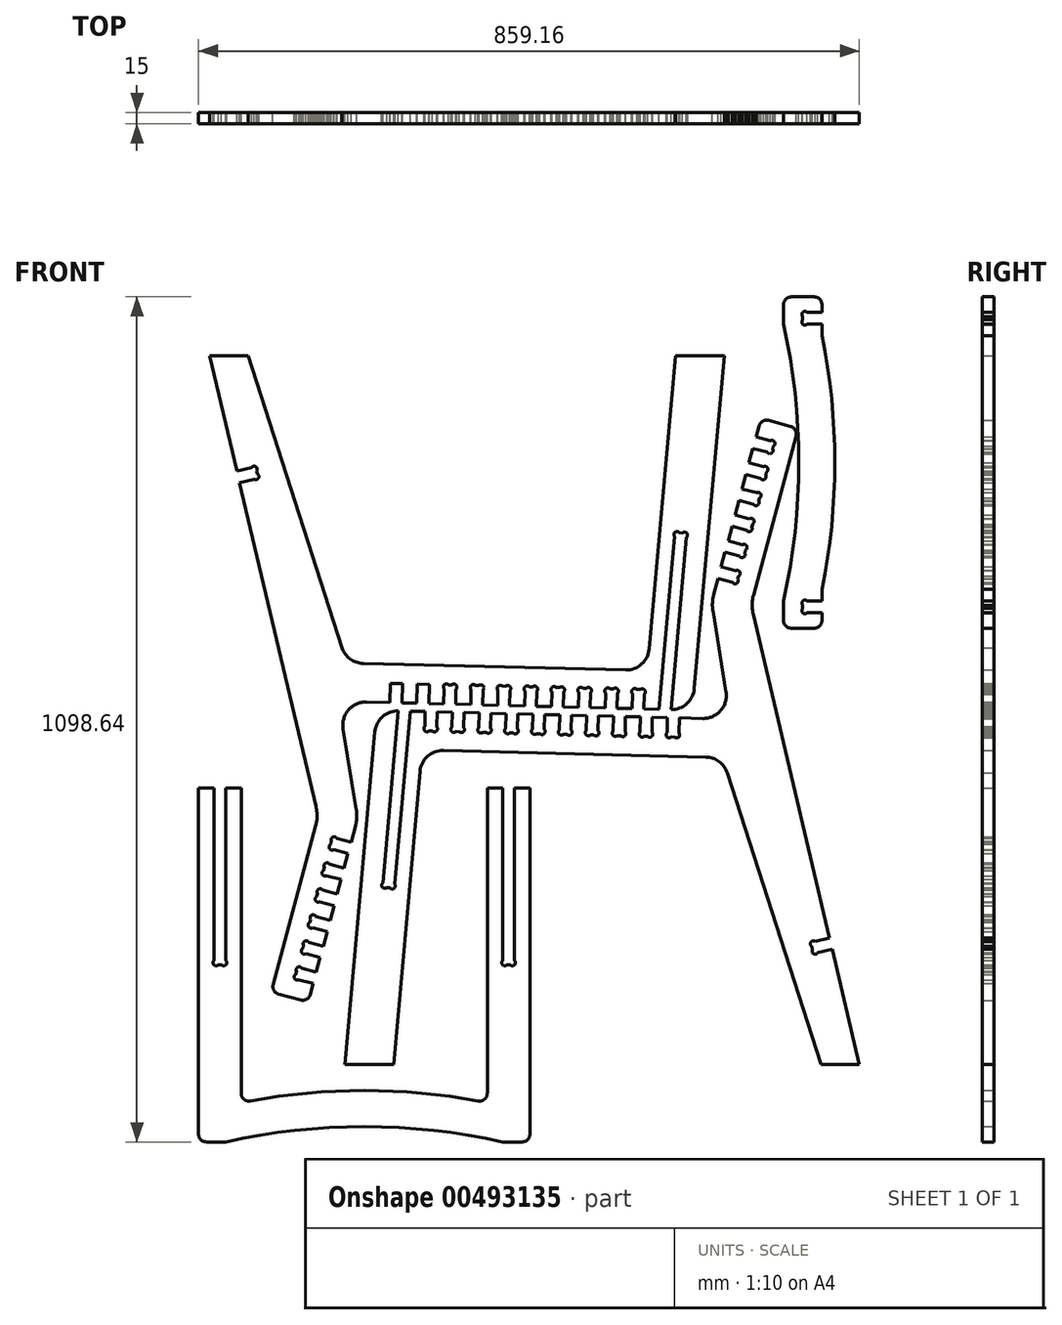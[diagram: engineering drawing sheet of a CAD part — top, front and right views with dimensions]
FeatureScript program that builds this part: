
annotation { "Feature Type Name" : "Feature", "Feature Type Description" : "" }
export const myFeature = defineFeature(function(context is Context, id is Id, definition is map)
    precondition{}
    {
        {
            var Q0;
            Q0=qCreatedBy(makeId("Front.planeOp"),FACE);
            var sketch = newSketch(context, id + "F0", { "sketchPlane" : qUnion([Q0])});
            skLineSegment(sketch, "E0", {"start": v(-375.2, 497.25) * mm, "end": v(-425.2, 497.25) * mm});
            skLineSegment(sketch, "E1", {"start": v(-425.2, 497.25) * mm, "end": v(-389.9, 347.46) * mm});
            skLineSegment(sketch, "E2", {"start": v(-389.9, 347.46) * mm, "end": v(-371.08, 351.9) * mm});
            skArc(sketch, "E3", {"start": v(-371.08, 351.9) * mm, "mid": v(-365.57, 353.2) * mm, "end": v(-364.28, 347.69) * mm});
            skLineSegment(sketch, "E4", {"start": v(-364.28, 347.69) * mm, "end": v(-363.34, 343.71) * mm});
            skArc(sketch, "E5", {"start": v(-363.34, 343.71) * mm, "mid": v(-362.04, 338.2) * mm, "end": v(-367.55, 336.91) * mm});
            skLineSegment(sketch, "E6", {"start": v(-367.55, 336.91) * mm, "end": v(-386.37, 332.48) * mm});
            skLineSegment(sketch, "E7", {"start": v(-386.37, 332.48) * mm, "end": v(-287.1, -88.96) * mm});
            skArc(sketch, "E8", {"start": v(-287.1, -88.96) * mm, "mid": v(-285.77, -101.18) * mm, "end": v(-287.47, -113.36) * mm});
            skLineSegment(sketch, "E9", {"start": v(-287.47, -113.36) * mm, "end": v(-342.89, -320.18) * mm});
            skArc(sketch, "E10", {"start": v(-342.89, -320.18) * mm, "mid": v(-341.89, -327.77) * mm, "end": v(-335.82, -332.42) * mm});
            skLineSegment(sketch, "E11", {"start": v(-335.82, -332.42) * mm, "end": v(-306.84, -340.19) * mm});
            skArc(sketch, "E12", {"start": v(-306.84, -340.19) * mm, "mid": v(-299.25, -339.19) * mm, "end": v(-294.6, -333.12) * mm});
            skLineSegment(sketch, "E13", {"start": v(-294.6, -333.12) * mm, "end": v(-290.77, -318.82) * mm});
            skLineSegment(sketch, "E14", {"start": v(-290.77, -318.82) * mm, "end": v(-309.45, -313.82) * mm});
            skArc(sketch, "E15", {"start": v(-309.45, -313.82) * mm, "mid": v(-314.91, -312.35) * mm, "end": v(-313.45, -306.9) * mm});
            skLineSegment(sketch, "E16", {"start": v(-313.45, -306.9) * mm, "end": v(-312.39, -302.94) * mm});
            skArc(sketch, "E17", {"start": v(-312.39, -302.94) * mm, "mid": v(-310.93, -297.48) * mm, "end": v(-305.46, -298.95) * mm});
            skLineSegment(sketch, "E18", {"start": v(-305.46, -298.95) * mm, "end": v(-286.78, -303.95) * mm});
            skLineSegment(sketch, "E19", {"start": v(-286.78, -303.95) * mm, "end": v(-281.7, -285.02) * mm});
            skLineSegment(sketch, "E20", {"start": v(-281.7, -285.02) * mm, "end": v(-300.39, -280.02) * mm});
            skArc(sketch, "E21", {"start": v(-300.39, -280.02) * mm, "mid": v(-305.85, -278.55) * mm, "end": v(-304.39, -273.09) * mm});
            skLineSegment(sketch, "E22", {"start": v(-304.39, -273.09) * mm, "end": v(-303.33, -269.14) * mm});
            skArc(sketch, "E23", {"start": v(-303.33, -269.14) * mm, "mid": v(-301.87, -263.68) * mm, "end": v(-296.4, -265.14) * mm});
            skLineSegment(sketch, "E24", {"start": v(-296.4, -265.14) * mm, "end": v(-277.72, -270.15) * mm});
            skLineSegment(sketch, "E25", {"start": v(-277.72, -270.15) * mm, "end": v(-272.65, -251.22) * mm});
            skLineSegment(sketch, "E26", {"start": v(-272.65, -251.22) * mm, "end": v(-291.33, -246.21) * mm});
            skArc(sketch, "E27", {"start": v(-291.33, -246.21) * mm, "mid": v(-296.8, -244.75) * mm, "end": v(-295.33, -239.29) * mm});
            skLineSegment(sketch, "E28", {"start": v(-295.33, -239.29) * mm, "end": v(-294.27, -235.34) * mm});
            skArc(sketch, "E29", {"start": v(-294.27, -235.34) * mm, "mid": v(-292.81, -229.88) * mm, "end": v(-287.35, -231.34) * mm});
            skLineSegment(sketch, "E30", {"start": v(-287.35, -231.34) * mm, "end": v(-268.66, -236.34) * mm});
            skLineSegment(sketch, "E31", {"start": v(-268.66, -236.34) * mm, "end": v(-263.6, -217.42) * mm});
            skLineSegment(sketch, "E32", {"start": v(-263.6, -217.42) * mm, "end": v(-282.27, -212.4) * mm});
            skArc(sketch, "E33", {"start": v(-282.27, -212.4) * mm, "mid": v(-287.74, -210.95) * mm, "end": v(-286.27, -205.48) * mm});
            skLineSegment(sketch, "E34", {"start": v(-286.27, -205.48) * mm, "end": v(-285.22, -201.54) * mm});
            skArc(sketch, "E35", {"start": v(-285.22, -201.54) * mm, "mid": v(-283.75, -196.07) * mm, "end": v(-278.29, -197.54) * mm});
            skLineSegment(sketch, "E36", {"start": v(-278.29, -197.54) * mm, "end": v(-259.6, -202.54) * mm});
            skLineSegment(sketch, "E37", {"start": v(-259.6, -202.54) * mm, "end": v(-254.54, -183.61) * mm});
            skLineSegment(sketch, "E38", {"start": v(-254.54, -183.61) * mm, "end": v(-273.22, -178.6) * mm});
            skArc(sketch, "E39", {"start": v(-273.22, -178.6) * mm, "mid": v(-278.68, -177.14) * mm, "end": v(-277.22, -171.68) * mm});
            skLineSegment(sketch, "E40", {"start": v(-277.22, -171.68) * mm, "end": v(-276.16, -167.73) * mm});
            skArc(sketch, "E41", {"start": v(-276.16, -167.73) * mm, "mid": v(-274.7, -162.27) * mm, "end": v(-269.23, -163.73) * mm});
            skLineSegment(sketch, "E42", {"start": v(-269.23, -163.73) * mm, "end": v(-250.55, -168.74) * mm});
            skLineSegment(sketch, "E43", {"start": v(-250.55, -168.74) * mm, "end": v(-245.48, -149.8) * mm});
            skLineSegment(sketch, "E44", {"start": v(-245.48, -149.8) * mm, "end": v(-264.16, -144.8) * mm});
            skArc(sketch, "E45", {"start": v(-264.16, -144.8) * mm, "mid": v(-269.62, -143.34) * mm, "end": v(-268.16, -137.88) * mm});
            skLineSegment(sketch, "E46", {"start": v(-268.16, -137.88) * mm, "end": v(-267.1, -133.93) * mm});
            skArc(sketch, "E47", {"start": v(-267.1, -133.93) * mm, "mid": v(-265.64, -128.47) * mm, "end": v(-260.17, -129.93) * mm});
            skLineSegment(sketch, "E48", {"start": v(-260.17, -129.93) * mm, "end": v(-241.5, -134.94) * mm});
            skLineSegment(sketch, "E49", {"start": v(-241.5, -134.94) * mm, "end": v(-235.8, -113.7) * mm});
            skArc(sketch, "E50", {"start": v(-235.8, -113.7) * mm, "mid": v(-234.15, -103.12) * mm, "end": v(-234.8, -92.43) * mm});
            skLineSegment(sketch, "E51", {"start": v(-234.8, -92.43) * mm, "end": v(-251.88, 12.44) * mm});
            skArc(sketch, "E52", {"start": v(-251.88, 12.44) * mm, "mid": v(-244.88, 36.98) * mm, "end": v(-221.53, 47.25) * mm});
            skLineSegment(sketch, "E53", {"start": v(-221.53, 47.25) * mm, "end": v(-190.95, 46.49) * mm});
            skLineSegment(sketch, "E54", {"start": v(-190.95, 46.49) * mm, "end": v(-190.33, 71.48) * mm});
            skLineSegment(sketch, "E55", {"start": v(-190.33, 71.48) * mm, "end": v(-174.93, 71.1) * mm});
            skLineSegment(sketch, "E56", {"start": v(-174.93, 71.1) * mm, "end": v(-175.56, 46.1) * mm});
            skLineSegment(sketch, "E57", {"start": v(-175.56, 46.1) * mm, "end": v(-155.97, 45.62) * mm});
            skLineSegment(sketch, "E58", {"start": v(-155.97, 45.62) * mm, "end": v(-155.34, 70.6) * mm});
            skLineSegment(sketch, "E59", {"start": v(-155.34, 70.6) * mm, "end": v(-139.95, 70.22) * mm});
            skLineSegment(sketch, "E60", {"start": v(-139.95, 70.22) * mm, "end": v(-140.57, 45.23) * mm});
            skLineSegment(sketch, "E61", {"start": v(-140.57, 45.23) * mm, "end": v(-120.98, 44.74) * mm});
            skLineSegment(sketch, "E62", {"start": v(-120.98, 44.74) * mm, "end": v(-120.5, 64.08) * mm});
            skArc(sketch, "E63", {"start": v(-120.5, 64.08) * mm, "mid": v(-120.36, 69.73) * mm, "end": v(-114.7, 69.6) * mm});
            skLineSegment(sketch, "E64", {"start": v(-114.7, 69.6) * mm, "end": v(-110.62, 69.5) * mm});
            skArc(sketch, "E65", {"start": v(-110.62, 69.5) * mm, "mid": v(-104.97, 69.35) * mm, "end": v(-105.1, 63.7) * mm});
            skLineSegment(sketch, "E66", {"start": v(-105.1, 63.7) * mm, "end": v(-105.59, 44.36) * mm});
            skLineSegment(sketch, "E67", {"start": v(-105.59, 44.36) * mm, "end": v(-86, 43.87) * mm});
            skLineSegment(sketch, "E68", {"start": v(-86, 43.87) * mm, "end": v(-85.51, 63.2) * mm});
            skArc(sketch, "E69", {"start": v(-85.51, 63.2) * mm, "mid": v(-85.37, 68.86) * mm, "end": v(-79.72, 68.72) * mm});
            skLineSegment(sketch, "E70", {"start": v(-79.72, 68.72) * mm, "end": v(-75.64, 68.62) * mm});
            skArc(sketch, "E71", {"start": v(-75.64, 68.62) * mm, "mid": v(-69.98, 68.48) * mm, "end": v(-70.12, 62.82) * mm});
            skLineSegment(sketch, "E72", {"start": v(-70.12, 62.82) * mm, "end": v(-70.6, 43.49) * mm});
            skLineSegment(sketch, "E73", {"start": v(-70.6, 43.49) * mm, "end": v(-51.01, 43) * mm});
            skLineSegment(sketch, "E74", {"start": v(-51.01, 43) * mm, "end": v(-50.53, 62.33) * mm});
            skArc(sketch, "E75", {"start": v(-50.53, 62.33) * mm, "mid": v(-50.39, 67.99) * mm, "end": v(-44.73, 67.85) * mm});
            skLineSegment(sketch, "E76", {"start": v(-44.73, 67.85) * mm, "end": v(-40.65, 67.75) * mm});
            skArc(sketch, "E77", {"start": v(-40.65, 67.75) * mm, "mid": v(-35, 67.6) * mm, "end": v(-35.14, 61.95) * mm});
            skLineSegment(sketch, "E78", {"start": v(-35.14, 61.95) * mm, "end": v(-35.62, 42.62) * mm});
            skLineSegment(sketch, "E79", {"start": v(-35.62, 42.62) * mm, "end": v(-16.03, 42.13) * mm});
            skLineSegment(sketch, "E80", {"start": v(-16.03, 42.13) * mm, "end": v(-15.55, 61.46) * mm});
            skArc(sketch, "E81", {"start": v(-15.55, 61.46) * mm, "mid": v(-15.4, 67.12) * mm, "end": v(-9.75, 66.98) * mm});
            skLineSegment(sketch, "E82", {"start": v(-9.75, 66.98) * mm, "end": v(-5.67, 66.87) * mm});
            skArc(sketch, "E83", {"start": v(-5.67, 66.87) * mm, "mid": v(-0.01, 66.73) * mm, "end": v(-0.15, 61.08) * mm});
            skLineSegment(sketch, "E84", {"start": v(-0.15, 61.08) * mm, "end": v(-0.63, 41.74) * mm});
            skLineSegment(sketch, "E85", {"start": v(-0.63, 41.74) * mm, "end": v(18.96, 41.26) * mm});
            skLineSegment(sketch, "E86", {"start": v(18.96, 41.26) * mm, "end": v(19.44, 60.6) * mm});
            skArc(sketch, "E87", {"start": v(19.44, 60.6) * mm, "mid": v(19.58, 66.24) * mm, "end": v(25.23, 66.1) * mm});
            skLineSegment(sketch, "E88", {"start": v(25.23, 66.1) * mm, "end": v(29.32, 66) * mm});
            skArc(sketch, "E89", {"start": v(29.32, 66) * mm, "mid": v(34.97, 65.86) * mm, "end": v(34.83, 60.2) * mm});
            skLineSegment(sketch, "E90", {"start": v(34.83, 60.2) * mm, "end": v(34.35, 40.87) * mm});
            skLineSegment(sketch, "E91", {"start": v(34.35, 40.87) * mm, "end": v(53.94, 40.38) * mm});
            skLineSegment(sketch, "E92", {"start": v(53.94, 40.38) * mm, "end": v(54.42, 59.72) * mm});
            skArc(sketch, "E93", {"start": v(54.42, 59.72) * mm, "mid": v(54.56, 65.37) * mm, "end": v(60.22, 65.23) * mm});
            skLineSegment(sketch, "E94", {"start": v(60.22, 65.23) * mm, "end": v(64.3, 65.13) * mm});
            skArc(sketch, "E95", {"start": v(64.3, 65.13) * mm, "mid": v(69.96, 64.99) * mm, "end": v(69.82, 59.33) * mm});
            skLineSegment(sketch, "E96", {"start": v(69.82, 59.33) * mm, "end": v(69.34, 40) * mm});
            skLineSegment(sketch, "E97", {"start": v(69.34, 40) * mm, "end": v(88.93, 39.51) * mm});
            skLineSegment(sketch, "E98", {"start": v(88.93, 39.51) * mm, "end": v(89.4, 58.85) * mm});
            skArc(sketch, "E99", {"start": v(89.4, 58.85) * mm, "mid": v(89.55, 64.5) * mm, "end": v(95.2, 64.36) * mm});
            skLineSegment(sketch, "E100", {"start": v(95.2, 64.36) * mm, "end": v(99.29, 64.26) * mm});
            skArc(sketch, "E101", {"start": v(99.29, 64.26) * mm, "mid": v(104.94, 64.12) * mm, "end": v(104.8, 58.46) * mm});
            skLineSegment(sketch, "E102", {"start": v(104.8, 58.46) * mm, "end": v(104.32, 39.13) * mm});
            skLineSegment(sketch, "E103", {"start": v(104.32, 39.13) * mm, "end": v(123.91, 38.64) * mm});
            skLineSegment(sketch, "E104", {"start": v(123.91, 38.64) * mm, "end": v(124.4, 57.97) * mm});
            skArc(sketch, "E105", {"start": v(124.4, 57.97) * mm, "mid": v(124.53, 63.63) * mm, "end": v(130.19, 63.49) * mm});
            skLineSegment(sketch, "E106", {"start": v(130.19, 63.49) * mm, "end": v(134.27, 63.39) * mm});
            skArc(sketch, "E107", {"start": v(134.27, 63.39) * mm, "mid": v(139.93, 63.24) * mm, "end": v(139.79, 57.6) * mm});
            skLineSegment(sketch, "E108", {"start": v(139.79, 57.6) * mm, "end": v(139.3, 38.26) * mm});
            skLineSegment(sketch, "E109", {"start": v(139.3, 38.26) * mm, "end": v(158.88, 37.77) * mm});
            skLineSegment(sketch, "E110", {"start": v(158.88, 37.77) * mm, "end": v(179.13, 262.38) * mm});
            skArc(sketch, "E111", {"start": v(179.13, 262.38) * mm, "mid": v(179.64, 268.01) * mm, "end": v(185.27, 267.5) * mm});
            skLineSegment(sketch, "E112", {"start": v(185.27, 267.5) * mm, "end": v(189.34, 267.14) * mm});
            skArc(sketch, "E113", {"start": v(189.34, 267.14) * mm, "mid": v(194.97, 266.63) * mm, "end": v(194.46, 261) * mm});
            skLineSegment(sketch, "E114", {"start": v(194.46, 261) * mm, "end": v(174.3, 37.38) * mm});
            skArc(sketch, "E115", {"start": v(174.3, 37.38) * mm, "mid": v(194.88, 45.05) * mm, "end": v(204.71, 64.68) * mm});
            skLineSegment(sketch, "E116", {"start": v(204.71, 64.68) * mm, "end": v(243.7, 497.25) * mm});
            skLineSegment(sketch, "E117", {"start": v(243.7, 497.25) * mm, "end": v(180.44, 497.25) * mm});
            skLineSegment(sketch, "E118", {"start": v(180.44, 497.25) * mm, "end": v(146.08, 116.15) * mm});
            skArc(sketch, "E119", {"start": v(146.08, 116.15) * mm, "mid": v(136.17, 96.45) * mm, "end": v(115.46, 88.86) * mm});
            skLineSegment(sketch, "E120", {"start": v(115.46, 88.86) * mm, "end": v(-225.61, 97.36) * mm});
            skArc(sketch, "E121", {"start": v(-225.61, 97.36) * mm, "mid": v(-242.67, 103.21) * mm, "end": v(-253.3, 117.79) * mm});
            skLineSegment(sketch, "E122", {"start": v(-253.3, 117.79) * mm, "end": v(-375.2, 497.25) * mm});
            skLineSegment(sketch, "E123", {"start": v(369.36, -424.14) * mm, "end": v(419.36, -424.14) * mm});
            skLineSegment(sketch, "E124", {"start": v(419.36, -424.14) * mm, "end": v(384.07, -274.36) * mm});
            skLineSegment(sketch, "E125", {"start": v(384.07, -274.36) * mm, "end": v(365.25, -278.8) * mm});
            skArc(sketch, "E126", {"start": v(365.25, -278.8) * mm, "mid": v(359.74, -280.09) * mm, "end": v(358.44, -274.58) * mm});
            skLineSegment(sketch, "E127", {"start": v(358.44, -274.58) * mm, "end": v(357.5, -270.6) * mm});
            skArc(sketch, "E128", {"start": v(357.5, -270.6) * mm, "mid": v(356.21, -265.1) * mm, "end": v(361.72, -263.8) * mm});
            skLineSegment(sketch, "E129", {"start": v(361.72, -263.8) * mm, "end": v(380.54, -259.37) * mm});
            skLineSegment(sketch, "E130", {"start": v(380.54, -259.37) * mm, "end": v(281.26, 162.06) * mm});
            skArc(sketch, "E131", {"start": v(281.26, 162.06) * mm, "mid": v(279.94, 174.29) * mm, "end": v(281.64, 186.46) * mm});
            skLineSegment(sketch, "E132", {"start": v(281.64, 186.46) * mm, "end": v(337.05, 393.28) * mm});
            skArc(sketch, "E133", {"start": v(337.05, 393.28) * mm, "mid": v(336.05, 400.87) * mm, "end": v(329.98, 405.53) * mm});
            skLineSegment(sketch, "E134", {"start": v(329.98, 405.53) * mm, "end": v(301, 413.3) * mm});
            skArc(sketch, "E135", {"start": v(301, 413.3) * mm, "mid": v(293.42, 412.3) * mm, "end": v(288.76, 406.22) * mm});
            skLineSegment(sketch, "E136", {"start": v(288.76, 406.22) * mm, "end": v(284.93, 391.93) * mm});
            skLineSegment(sketch, "E137", {"start": v(284.93, 391.93) * mm, "end": v(303.61, 386.92) * mm});
            skArc(sketch, "E138", {"start": v(303.61, 386.92) * mm, "mid": v(309.08, 385.46) * mm, "end": v(307.61, 380) * mm});
            skLineSegment(sketch, "E139", {"start": v(307.61, 380) * mm, "end": v(306.56, 376.05) * mm});
            skArc(sketch, "E140", {"start": v(306.56, 376.05) * mm, "mid": v(305.1, 370.59) * mm, "end": v(299.63, 372.05) * mm});
            skLineSegment(sketch, "E141", {"start": v(299.63, 372.05) * mm, "end": v(280.95, 377.06) * mm});
            skLineSegment(sketch, "E142", {"start": v(280.95, 377.06) * mm, "end": v(275.87, 358.13) * mm});
            skLineSegment(sketch, "E143", {"start": v(275.87, 358.13) * mm, "end": v(294.56, 353.12) * mm});
            skArc(sketch, "E144", {"start": v(294.56, 353.12) * mm, "mid": v(300.02, 351.66) * mm, "end": v(298.56, 346.2) * mm});
            skLineSegment(sketch, "E145", {"start": v(298.56, 346.2) * mm, "end": v(297.5, 342.25) * mm});
            skArc(sketch, "E146", {"start": v(297.5, 342.25) * mm, "mid": v(296.03, 336.78) * mm, "end": v(290.57, 338.25) * mm});
            skLineSegment(sketch, "E147", {"start": v(290.57, 338.25) * mm, "end": v(271.89, 343.25) * mm});
            skLineSegment(sketch, "E148", {"start": v(271.89, 343.25) * mm, "end": v(266.82, 324.32) * mm});
            skLineSegment(sketch, "E149", {"start": v(266.82, 324.32) * mm, "end": v(285.5, 319.32) * mm});
            skArc(sketch, "E150", {"start": v(285.5, 319.32) * mm, "mid": v(290.96, 317.85) * mm, "end": v(289.5, 312.4) * mm});
            skLineSegment(sketch, "E151", {"start": v(289.5, 312.4) * mm, "end": v(288.44, 308.44) * mm});
            skArc(sketch, "E152", {"start": v(288.44, 308.44) * mm, "mid": v(286.98, 302.98) * mm, "end": v(281.51, 304.44) * mm});
            skLineSegment(sketch, "E153", {"start": v(281.51, 304.44) * mm, "end": v(262.83, 309.45) * mm});
            skLineSegment(sketch, "E154", {"start": v(262.83, 309.45) * mm, "end": v(257.76, 290.52) * mm});
            skLineSegment(sketch, "E155", {"start": v(257.76, 290.52) * mm, "end": v(276.44, 285.51) * mm});
            skArc(sketch, "E156", {"start": v(276.44, 285.51) * mm, "mid": v(281.9, 284.05) * mm, "end": v(280.44, 278.59) * mm});
            skLineSegment(sketch, "E157", {"start": v(280.44, 278.59) * mm, "end": v(279.38, 274.64) * mm});
            skArc(sketch, "E158", {"start": v(279.38, 274.64) * mm, "mid": v(277.92, 269.18) * mm, "end": v(272.46, 270.64) * mm});
            skLineSegment(sketch, "E159", {"start": v(272.46, 270.64) * mm, "end": v(253.77, 275.65) * mm});
            skLineSegment(sketch, "E160", {"start": v(253.77, 275.65) * mm, "end": v(248.7, 256.72) * mm});
            skLineSegment(sketch, "E161", {"start": v(248.7, 256.72) * mm, "end": v(267.38, 251.71) * mm});
            skArc(sketch, "E162", {"start": v(267.38, 251.71) * mm, "mid": v(272.85, 250.25) * mm, "end": v(271.38, 244.78) * mm});
            skLineSegment(sketch, "E163", {"start": v(271.38, 244.78) * mm, "end": v(270.33, 240.84) * mm});
            skArc(sketch, "E164", {"start": v(270.33, 240.84) * mm, "mid": v(268.86, 235.37) * mm, "end": v(263.4, 236.84) * mm});
            skLineSegment(sketch, "E165", {"start": v(263.4, 236.84) * mm, "end": v(244.72, 241.84) * mm});
            skLineSegment(sketch, "E166", {"start": v(244.72, 241.84) * mm, "end": v(239.64, 222.91) * mm});
            skLineSegment(sketch, "E167", {"start": v(239.64, 222.91) * mm, "end": v(258.33, 217.9) * mm});
            skArc(sketch, "E168", {"start": v(258.33, 217.9) * mm, "mid": v(263.79, 216.44) * mm, "end": v(262.33, 210.98) * mm});
            skLineSegment(sketch, "E169", {"start": v(262.33, 210.98) * mm, "end": v(261.27, 207.03) * mm});
            skArc(sketch, "E170", {"start": v(261.27, 207.03) * mm, "mid": v(259.8, 201.57) * mm, "end": v(254.34, 203.03) * mm});
            skLineSegment(sketch, "E171", {"start": v(254.34, 203.03) * mm, "end": v(235.66, 208.04) * mm});
            skLineSegment(sketch, "E172", {"start": v(235.66, 208.04) * mm, "end": v(229.97, 186.8) * mm});
            skArc(sketch, "E173", {"start": v(229.97, 186.8) * mm, "mid": v(228.32, 176.22) * mm, "end": v(228.96, 165.54) * mm});
            skLineSegment(sketch, "E174", {"start": v(228.96, 165.54) * mm, "end": v(246.05, 60.66) * mm});
            skArc(sketch, "E175", {"start": v(246.05, 60.66) * mm, "mid": v(239.05, 36.13) * mm, "end": v(215.7, 25.86) * mm});
            skLineSegment(sketch, "E176", {"start": v(215.7, 25.86) * mm, "end": v(185.12, 26.62) * mm});
            skLineSegment(sketch, "E177", {"start": v(185.12, 26.62) * mm, "end": v(184.64, 7.28) * mm});
            skArc(sketch, "E178", {"start": v(184.64, 7.28) * mm, "mid": v(184.5, 1.63) * mm, "end": v(178.84, 1.77) * mm});
            skLineSegment(sketch, "E179", {"start": v(178.84, 1.77) * mm, "end": v(174.76, 1.87) * mm});
            skArc(sketch, "E180", {"start": v(174.76, 1.87) * mm, "mid": v(169.1, 2.01) * mm, "end": v(169.24, 7.67) * mm});
            skLineSegment(sketch, "E181", {"start": v(169.24, 7.67) * mm, "end": v(169.72, 27) * mm});
            skLineSegment(sketch, "E182", {"start": v(169.72, 27) * mm, "end": v(150.13, 27.49) * mm});
            skLineSegment(sketch, "E183", {"start": v(150.13, 27.49) * mm, "end": v(149.65, 8.15) * mm});
            skArc(sketch, "E184", {"start": v(149.65, 8.15) * mm, "mid": v(149.51, 2.5) * mm, "end": v(143.86, 2.64) * mm});
            skLineSegment(sketch, "E185", {"start": v(143.86, 2.64) * mm, "end": v(139.77, 2.74) * mm});
            skArc(sketch, "E186", {"start": v(139.77, 2.74) * mm, "mid": v(134.12, 2.88) * mm, "end": v(134.26, 8.54) * mm});
            skLineSegment(sketch, "E187", {"start": v(134.26, 8.54) * mm, "end": v(134.74, 27.87) * mm});
            skLineSegment(sketch, "E188", {"start": v(134.74, 27.87) * mm, "end": v(115.15, 28.36) * mm});
            skLineSegment(sketch, "E189", {"start": v(115.15, 28.36) * mm, "end": v(114.67, 9.03) * mm});
            skArc(sketch, "E190", {"start": v(114.67, 9.03) * mm, "mid": v(114.53, 3.37) * mm, "end": v(108.87, 3.51) * mm});
            skLineSegment(sketch, "E191", {"start": v(108.87, 3.51) * mm, "end": v(104.79, 3.62) * mm});
            skArc(sketch, "E192", {"start": v(104.79, 3.62) * mm, "mid": v(99.13, 3.76) * mm, "end": v(99.27, 9.41) * mm});
            skLineSegment(sketch, "E193", {"start": v(99.27, 9.41) * mm, "end": v(99.76, 28.75) * mm});
            skLineSegment(sketch, "E194", {"start": v(99.76, 28.75) * mm, "end": v(80.16, 29.23) * mm});
            skLineSegment(sketch, "E195", {"start": v(80.16, 29.23) * mm, "end": v(79.68, 9.9) * mm});
            skArc(sketch, "E196", {"start": v(79.68, 9.9) * mm, "mid": v(79.54, 4.24) * mm, "end": v(73.89, 4.39) * mm});
            skLineSegment(sketch, "E197", {"start": v(73.89, 4.39) * mm, "end": v(69.8, 4.49) * mm});
            skArc(sketch, "E198", {"start": v(69.8, 4.49) * mm, "mid": v(64.15, 4.63) * mm, "end": v(64.29, 10.28) * mm});
            skLineSegment(sketch, "E199", {"start": v(64.29, 10.28) * mm, "end": v(64.77, 29.62) * mm});
            skLineSegment(sketch, "E200", {"start": v(64.77, 29.62) * mm, "end": v(45.18, 30.1) * mm});
            skLineSegment(sketch, "E201", {"start": v(45.18, 30.1) * mm, "end": v(44.7, 10.77) * mm});
            skArc(sketch, "E202", {"start": v(44.7, 10.77) * mm, "mid": v(44.56, 5.12) * mm, "end": v(38.9, 5.26) * mm});
            skLineSegment(sketch, "E203", {"start": v(38.9, 5.26) * mm, "end": v(34.82, 5.36) * mm});
            skArc(sketch, "E204", {"start": v(34.82, 5.36) * mm, "mid": v(29.16, 5.5) * mm, "end": v(29.3, 11.15) * mm});
            skLineSegment(sketch, "E205", {"start": v(29.3, 11.15) * mm, "end": v(29.79, 30.49) * mm});
            skLineSegment(sketch, "E206", {"start": v(29.79, 30.49) * mm, "end": v(10.2, 30.98) * mm});
            skLineSegment(sketch, "E207", {"start": v(10.2, 30.98) * mm, "end": v(9.71, 11.64) * mm});
            skArc(sketch, "E208", {"start": v(9.71, 11.64) * mm, "mid": v(9.57, 5.99) * mm, "end": v(3.92, 6.13) * mm});
            skLineSegment(sketch, "E209", {"start": v(3.92, 6.13) * mm, "end": v(-0.17, 6.23) * mm});
            skArc(sketch, "E210", {"start": v(-0.17, 6.23) * mm, "mid": v(-5.82, 6.37) * mm, "end": v(-5.68, 12.03) * mm});
            skLineSegment(sketch, "E211", {"start": v(-5.68, 12.03) * mm, "end": v(-5.2, 31.36) * mm});
            skLineSegment(sketch, "E212", {"start": v(-5.2, 31.36) * mm, "end": v(-24.8, 31.85) * mm});
            skLineSegment(sketch, "E213", {"start": v(-24.8, 31.85) * mm, "end": v(-25.27, 12.52) * mm});
            skArc(sketch, "E214", {"start": v(-25.27, 12.52) * mm, "mid": v(-25.41, 6.86) * mm, "end": v(-31.07, 7) * mm});
            skLineSegment(sketch, "E215", {"start": v(-31.07, 7) * mm, "end": v(-35.15, 7.1) * mm});
            skArc(sketch, "E216", {"start": v(-35.15, 7.1) * mm, "mid": v(-40.8, 7.24) * mm, "end": v(-40.67, 12.9) * mm});
            skLineSegment(sketch, "E217", {"start": v(-40.67, 12.9) * mm, "end": v(-40.18, 32.23) * mm});
            skLineSegment(sketch, "E218", {"start": v(-40.18, 32.23) * mm, "end": v(-59.78, 32.72) * mm});
            skLineSegment(sketch, "E219", {"start": v(-59.78, 32.72) * mm, "end": v(-60.26, 13.39) * mm});
            skArc(sketch, "E220", {"start": v(-60.26, 13.39) * mm, "mid": v(-60.4, 7.73) * mm, "end": v(-66.05, 7.87) * mm});
            skLineSegment(sketch, "E221", {"start": v(-66.05, 7.87) * mm, "end": v(-70.14, 7.98) * mm});
            skArc(sketch, "E222", {"start": v(-70.14, 7.98) * mm, "mid": v(-75.8, 8.12) * mm, "end": v(-75.65, 13.77) * mm});
            skLineSegment(sketch, "E223", {"start": v(-75.65, 13.77) * mm, "end": v(-75.17, 33.1) * mm});
            skLineSegment(sketch, "E224", {"start": v(-75.17, 33.1) * mm, "end": v(-94.76, 33.6) * mm});
            skLineSegment(sketch, "E225", {"start": v(-94.76, 33.6) * mm, "end": v(-95.24, 14.26) * mm});
            skArc(sketch, "E226", {"start": v(-95.24, 14.26) * mm, "mid": v(-95.38, 8.6) * mm, "end": v(-101.04, 8.75) * mm});
            skLineSegment(sketch, "E227", {"start": v(-101.04, 8.75) * mm, "end": v(-105.12, 8.85) * mm});
            skArc(sketch, "E228", {"start": v(-105.12, 8.85) * mm, "mid": v(-110.78, 8.99) * mm, "end": v(-110.64, 14.64) * mm});
            skLineSegment(sketch, "E229", {"start": v(-110.64, 14.64) * mm, "end": v(-110.15, 33.98) * mm});
            skLineSegment(sketch, "E230", {"start": v(-110.15, 33.98) * mm, "end": v(-129.74, 34.47) * mm});
            skLineSegment(sketch, "E231", {"start": v(-129.74, 34.47) * mm, "end": v(-130.23, 15.13) * mm});
            skArc(sketch, "E232", {"start": v(-130.23, 15.13) * mm, "mid": v(-130.37, 9.48) * mm, "end": v(-136.02, 9.62) * mm});
            skLineSegment(sketch, "E233", {"start": v(-136.02, 9.62) * mm, "end": v(-140.1, 9.72) * mm});
            skArc(sketch, "E234", {"start": v(-140.1, 9.72) * mm, "mid": v(-145.76, 9.86) * mm, "end": v(-145.62, 15.52) * mm});
            skLineSegment(sketch, "E235", {"start": v(-145.62, 15.52) * mm, "end": v(-145.14, 34.85) * mm});
            skLineSegment(sketch, "E236", {"start": v(-145.14, 34.85) * mm, "end": v(-164.71, 35.34) * mm});
            skLineSegment(sketch, "E237", {"start": v(-164.71, 35.34) * mm, "end": v(-184.96, -189.27) * mm});
            skArc(sketch, "E238", {"start": v(-184.96, -189.27) * mm, "mid": v(-185.47, -194.9) * mm, "end": v(-191.1, -194.4) * mm});
            skLineSegment(sketch, "E239", {"start": v(-191.1, -194.4) * mm, "end": v(-195.17, -194.03) * mm});
            skArc(sketch, "E240", {"start": v(-195.17, -194.03) * mm, "mid": v(-200.8, -193.52) * mm, "end": v(-200.3, -187.89) * mm});
            skLineSegment(sketch, "E241", {"start": v(-200.3, -187.89) * mm, "end": v(-180.14, 35.72) * mm});
            skArc(sketch, "E242", {"start": v(-180.14, 35.72) * mm, "mid": v(-200.7, 28.05) * mm, "end": v(-210.55, 8.42) * mm});
            skLineSegment(sketch, "E243", {"start": v(-210.55, 8.42) * mm, "end": v(-249.54, -424.14) * mm});
            skLineSegment(sketch, "E244", {"start": v(-249.54, -424.14) * mm, "end": v(-186.27, -424.14) * mm});
            skLineSegment(sketch, "E245", {"start": v(-186.27, -424.14) * mm, "end": v(-151.92, -43.05) * mm});
            skArc(sketch, "E246", {"start": v(-151.92, -43.05) * mm, "mid": v(-142, -23.35) * mm, "end": v(-121.3, -15.75) * mm});
            skLineSegment(sketch, "E247", {"start": v(-121.3, -15.75) * mm, "end": v(219.78, -24.26) * mm});
            skArc(sketch, "E248", {"start": v(219.78, -24.26) * mm, "mid": v(236.84, -30.1) * mm, "end": v(247.46, -44.68) * mm});
            skLineSegment(sketch, "E249", {"start": v(247.46, -44.68) * mm, "end": v(369.36, -424.14) * mm});
            skLineSegment(sketch, "E250", {"start": v(-9.05, -64.32) * mm, "end": v(-29.05, -64.32) * mm});
            skLineSegment(sketch, "E251", {"start": v(-29.05, -64.32) * mm, "end": v(-29.05, -288.85) * mm});
            skArc(sketch, "E252", {"start": v(-29.05, -288.85) * mm, "mid": v(-29.05, -294.5) * mm, "end": v(-34.7, -294.5) * mm});
            skLineSegment(sketch, "E253", {"start": v(-34.7, -294.5) * mm, "end": v(-38.8, -294.5) * mm});
            skArc(sketch, "E254", {"start": v(-38.8, -294.5) * mm, "mid": v(-44.45, -294.5) * mm, "end": v(-44.45, -288.85) * mm});
            skLineSegment(sketch, "E255", {"start": v(-44.45, -288.85) * mm, "end": v(-44.45, -64.32) * mm});
            skLineSegment(sketch, "E256", {"start": v(-44.45, -64.32) * mm, "end": v(-64.45, -64.32) * mm});
            skLineSegment(sketch, "E257", {"start": v(-64.45, -64.32) * mm, "end": v(-64.45, -461.6) * mm});
            skArc(sketch, "E258", {"start": v(-64.45, -461.6) * mm, "mid": v(-68.05, -469.29) * mm, "end": v(-76.25, -471.44) * mm});
            skArc(sketch, "E259", {"start": v(-76.25, -471.44) * mm, "mid": v(-224.43, -457.94) * mm, "end": v(-372.6, -471.44) * mm});
            skArc(sketch, "E260", {"start": v(-372.6, -471.44) * mm, "mid": v(-380.8, -469.29) * mm, "end": v(-384.4, -461.6) * mm});
            skLineSegment(sketch, "E261", {"start": v(-384.4, -461.6) * mm, "end": v(-384.4, -64.32) * mm});
            skLineSegment(sketch, "E262", {"start": v(-384.4, -64.32) * mm, "end": v(-404.4, -64.32) * mm});
            skLineSegment(sketch, "E263", {"start": v(-404.4, -64.32) * mm, "end": v(-404.4, -288.85) * mm});
            skArc(sketch, "E264", {"start": v(-404.4, -288.85) * mm, "mid": v(-404.4, -294.5) * mm, "end": v(-410.06, -294.5) * mm});
            skLineSegment(sketch, "E265", {"start": v(-410.06, -294.5) * mm, "end": v(-414.14, -294.5) * mm});
            skArc(sketch, "E266", {"start": v(-414.14, -294.5) * mm, "mid": v(-419.8, -294.5) * mm, "end": v(-419.8, -288.85) * mm});
            skLineSegment(sketch, "E267", {"start": v(-419.8, -288.85) * mm, "end": v(-419.8, -64.32) * mm});
            skLineSegment(sketch, "E268", {"start": v(-419.8, -64.32) * mm, "end": v(-439.8, -64.32) * mm});
            skLineSegment(sketch, "E269", {"start": v(-439.8, -64.32) * mm, "end": v(-439.8, -514.7) * mm});
            skArc(sketch, "E270", {"start": v(-439.8, -514.7) * mm, "mid": v(-436.87, -521.77) * mm, "end": v(-429.8, -524.7) * mm});
            skLineSegment(sketch, "E271", {"start": v(-429.8, -524.7) * mm, "end": v(-404.37, -524.7) * mm});
            skArc(sketch, "E272", {"start": v(-404.37, -524.7) * mm, "mid": v(-224.43, -504.7) * mm, "end": v(-44.48, -524.7) * mm});
            skLineSegment(sketch, "E273", {"start": v(-44.48, -524.7) * mm, "end": v(-19.05, -524.7) * mm});
            skArc(sketch, "E274", {"start": v(-19.05, -524.7) * mm, "mid": v(-11.98, -521.77) * mm, "end": v(-9.05, -514.7) * mm});
            skLineSegment(sketch, "E275", {"start": v(-9.05, -514.7) * mm, "end": v(-9.05, -64.32) * mm});
            skLineSegment(sketch, "E276", {"start": v(320.68, 178.62) * mm, "end": v(320.68, 153.19) * mm});
            skArc(sketch, "E277", {"start": v(320.68, 153.19) * mm, "mid": v(323.6, 146.12) * mm, "end": v(330.67, 143.2) * mm});
            skLineSegment(sketch, "E278", {"start": v(330.67, 143.2) * mm, "end": v(360.66, 143.2) * mm});
            skArc(sketch, "E279", {"start": v(360.66, 143.2) * mm, "mid": v(367.73, 146.12) * mm, "end": v(370.66, 153.19) * mm});
            skLineSegment(sketch, "E280", {"start": v(370.66, 153.19) * mm, "end": v(370.66, 163.19) * mm});
            skLineSegment(sketch, "E281", {"start": v(370.66, 163.19) * mm, "end": v(351.32, 163.19) * mm});
            skArc(sketch, "E282", {"start": v(351.32, 163.19) * mm, "mid": v(345.67, 163.19) * mm, "end": v(345.67, 168.84) * mm});
            skLineSegment(sketch, "E283", {"start": v(345.67, 168.84) * mm, "end": v(345.67, 172.93) * mm});
            skArc(sketch, "E284", {"start": v(345.67, 172.93) * mm, "mid": v(345.67, 178.59) * mm, "end": v(351.32, 178.59) * mm});
            skLineSegment(sketch, "E285", {"start": v(351.32, 178.59) * mm, "end": v(370.66, 178.59) * mm});
            skLineSegment(sketch, "E286", {"start": v(370.66, 178.59) * mm, "end": v(370.66, 193.58) * mm});
            skArc(sketch, "E287", {"start": v(370.66, 193.58) * mm, "mid": v(387.44, 358.56) * mm, "end": v(370.66, 523.54) * mm});
            skLineSegment(sketch, "E288", {"start": v(370.66, 523.54) * mm, "end": v(370.66, 538.54) * mm});
            skLineSegment(sketch, "E289", {"start": v(370.66, 538.54) * mm, "end": v(351.32, 538.54) * mm});
            skArc(sketch, "E290", {"start": v(351.32, 538.54) * mm, "mid": v(345.67, 538.54) * mm, "end": v(345.67, 544.2) * mm});
            skLineSegment(sketch, "E291", {"start": v(345.67, 544.2) * mm, "end": v(345.67, 548.28) * mm});
            skArc(sketch, "E292", {"start": v(345.67, 548.28) * mm, "mid": v(345.67, 553.94) * mm, "end": v(351.32, 553.94) * mm});
            skLineSegment(sketch, "E293", {"start": v(351.32, 553.94) * mm, "end": v(370.66, 553.94) * mm});
            skLineSegment(sketch, "E294", {"start": v(370.66, 553.94) * mm, "end": v(370.66, 563.94) * mm});
            skArc(sketch, "E295", {"start": v(370.66, 563.94) * mm, "mid": v(367.73, 571) * mm, "end": v(360.66, 573.94) * mm});
            skLineSegment(sketch, "E296", {"start": v(360.66, 573.94) * mm, "end": v(330.67, 573.94) * mm});
            skArc(sketch, "E297", {"start": v(330.67, 573.94) * mm, "mid": v(323.6, 571) * mm, "end": v(320.68, 563.94) * mm});
            skLineSegment(sketch, "E298", {"start": v(320.68, 563.94) * mm, "end": v(320.68, 538.5) * mm});
            skArc(sketch, "E299", {"start": v(320.68, 538.5) * mm, "mid": v(340.67, 358.56) * mm, "end": v(320.68, 178.62) * mm});
            skSolve(sketch);
        }
        {
            var Q0;
            Q0=qSketchRegion(id+"F0",true);
            extrude(context, id + "F1", {"entities" : qUnion([Q0]), "depth" : 15 * mm});
        }
    });
